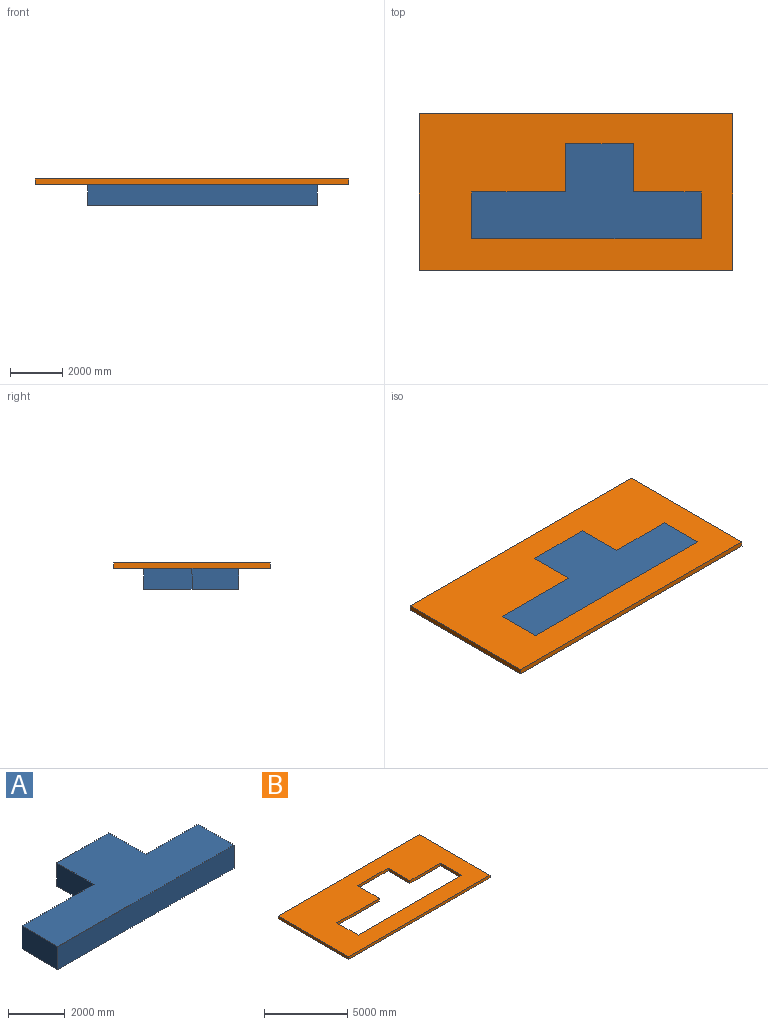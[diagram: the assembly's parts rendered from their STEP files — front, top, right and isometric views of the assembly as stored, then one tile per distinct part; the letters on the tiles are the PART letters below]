
ASSEMBLY  parts=2 mates=1
PART A: 10 faces, bbox 8800x3650x1000 mm
  f0: plane 2600x1000mm, normal (0,1,0), area 2600000mm2, adj f1,f7,f8,f9
  f1: plane 1850x1000mm, normal (1,0,0), area 1850000mm2, adj f0,f2,f8,f9
  f2: plane 2600x1000mm, normal (0,1,0), area 2600000mm2, adj f1,f3,f8,f9
  f3: plane 1850x1000mm, normal (-1,0,0), area 1850000mm2, adj f2,f4,f8,f9
  f4: plane 3600x1000mm, normal (0,1,0), area 3600000mm2, adj f3,f5,f8,f9
  f5: plane 1800x1000mm, normal (-1,0,0), area 1800000mm2, adj f4,f6,f8,f9
  f6: plane 8800x1000mm, normal (0,-1,0), area 8800000mm2, adj f5,f7,f8,f9
  f7: plane 1800x1000mm, normal (1,0,0), area 1800000mm2, adj f0,f6,f8,f9
  f8: plane 8800x3650mm, normal (0,0,1), area 20650000mm2, adj f0,f1,f2,f3,f4,f5,f6,f7
  f9: plane 8800x3650mm, normal (0,0,-1), area 20650000mm2, adj f0,f1,f2,f3,f4,f5,f6,f7
PART B: 14 faces, bbox 12000x6000x200 mm
  f0: plane 12000x6000mm, normal (0,0,1), area 51350000mm2, adj f2,f3,f4,f5,f6,f7,f8,f9
  f1: plane 12000x6000mm, normal (0,0,-1), area 51350000mm2, adj f2,f3,f4,f5,f6,f7,f8,f9
  f2: plane 12000x200mm, normal (0,-1,0), area 2400000mm2, adj f0,f1,f3,f5
  f3: plane 6000x200mm, normal (1,0,0), area 1200000mm2, adj f0,f1,f2,f4
  f4: plane 12000x200mm, normal (0,1,0), area 2400000mm2, adj f0,f1,f3,f5
  f5: plane 6000x200mm, normal (-1,0,0), area 1200000mm2, adj f0,f1,f2,f4
  f6: plane 2600x200mm, normal (0,-1,0), area 520000mm2, adj f0,f1,f7,f13
  f7: plane 1850x200mm, normal (1,0,0), area 370000mm2, adj f0,f1,f6,f8
  f8: plane 3600x200mm, normal (0,-1,0), area 720000mm2, adj f0,f1,f7,f9
  f9: plane 1800x200mm, normal (1,0,0), area 360000mm2, adj f0,f1,f8,f10
  f10: plane 8800x200mm, normal (0,1,0), area 1760000mm2, adj f0,f1,f9,f11
  f11: plane 1800x200mm, normal (-1,0,0), area 360000mm2, adj f0,f1,f10,f12
  f12: plane 2600x200mm, normal (0,-1,0), area 520000mm2, adj f0,f1,f11,f13
  f13: plane 1850x200mm, normal (-1,0,0), area 370000mm2, adj f0,f1,f6,f12
PLACE A rot(axis=(-0.88,-0.47,-0.08),0deg) t=(1885.35,175.44,-1374.29)mm
PLACE B rot(axis=(-0.88,-0.47,-0.08),0deg) t=(-352.12,217.99,-574.29)mm
MATE fastened A.f8 <-> B.f0  axis (0,0,-1) through (-752.12,2067.99,-374.29)mm
